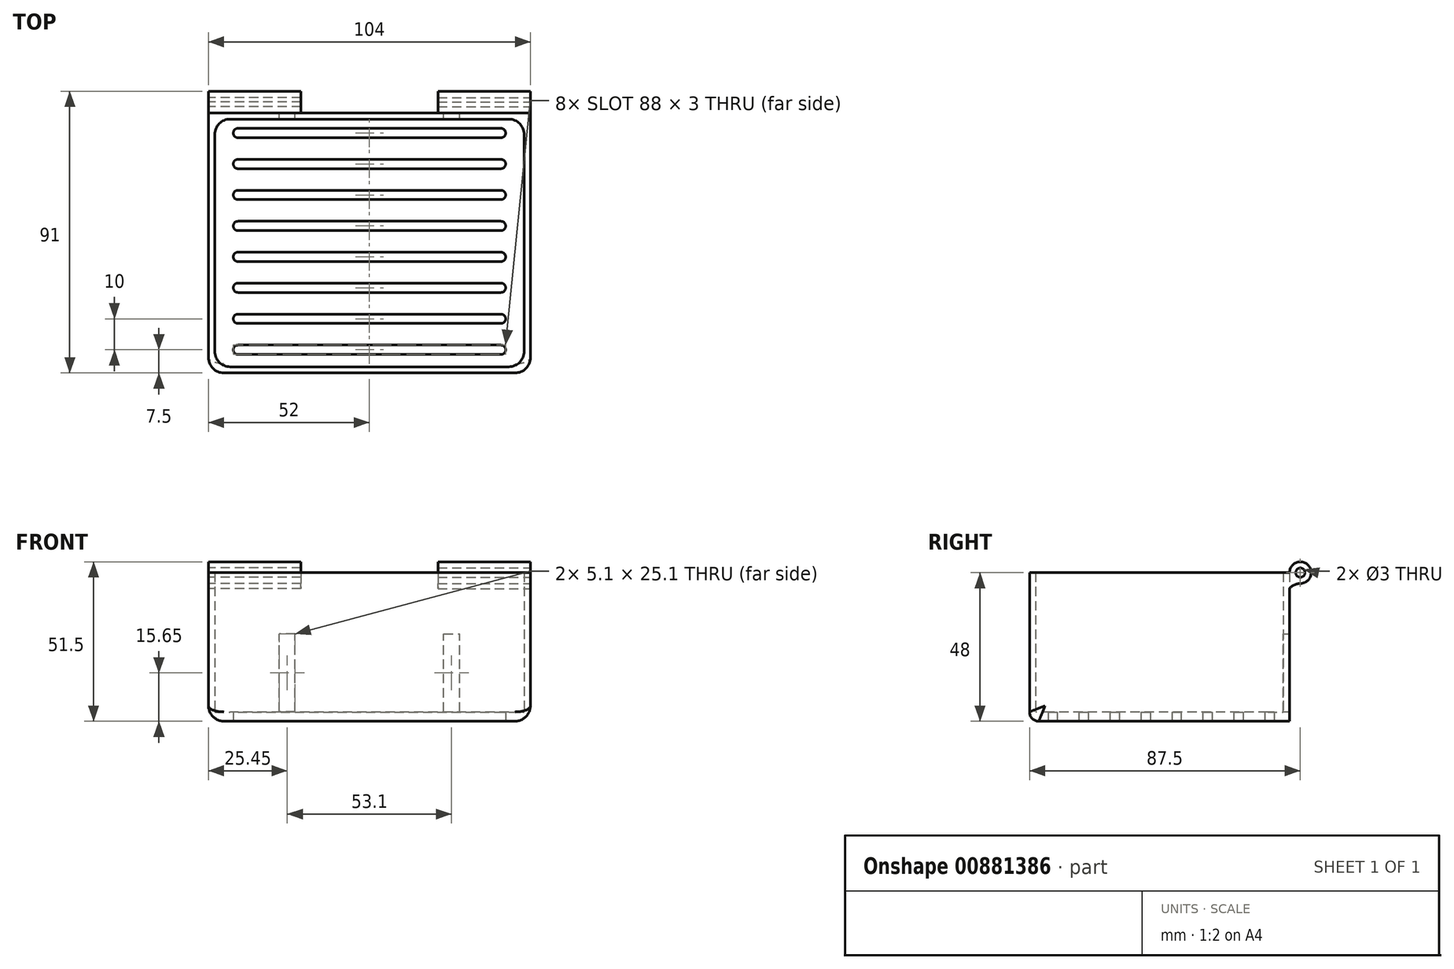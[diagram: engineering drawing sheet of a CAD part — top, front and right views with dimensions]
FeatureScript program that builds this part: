
annotation { "Feature Type Name" : "Feature", "Feature Type Description" : "" }
export const myFeature = defineFeature(function(context is Context, id is Id, definition is map)
    precondition{}
    {
        {
            var Q0;
            Q0=qCreatedBy(makeId("Top.planeOp"),FACE);
            var sketch = newSketch(context, id + "F0", { "sketchPlane" : qUnion([Q0])});
            skLineSegment(sketch, "E0.bottom", {"start": v(50, 40) * mm, "end": v(-50, 40) * mm});
            skLineSegment(sketch, "E0.top", {"start": v(50, -40) * mm, "end": v(-50, -40) * mm});
            skLineSegment(sketch, "E0.left", {"start": v(50, 40) * mm, "end": v(50, -40) * mm});
            skLineSegment(sketch, "E0.right", {"start": v(-50, 40) * mm, "end": v(-50, -40) * mm});
            skPoint(sketch, "E0.middle", {"position": v(0, 0) * mm});
            skLineSegment(sketch, "E1.bottom", {"start": v(52, 42) * mm, "end": v(-52, 42) * mm});
            skLineSegment(sketch, "E1.top", {"start": v(52, -42) * mm, "end": v(-52, -42) * mm});
            skLineSegment(sketch, "E1.left", {"start": v(52, 42) * mm, "end": v(52, -42) * mm});
            skLineSegment(sketch, "E1.right", {"start": v(-52, 42) * mm, "end": v(-52, -42) * mm});
            skLineSegment(sketch, "E2.bottom", {"start": v(-42.5, 37) * mm, "end": v(42.5, 37) * mm});
            skLineSegment(sketch, "E2.top", {"start": v(-42.5, 34) * mm, "end": v(42.5, 34) * mm});
            skPoint(sketch, "E3", {"position": v(0, 37) * mm});
            skArc(sketch, "E4", {"start": v(-42.5, 37) * mm, "mid": v(-44, 35.5) * mm, "end": v(-42.5, 34) * mm});
            skArc(sketch, "E5", {"start": v(42.5, 34) * mm, "mid": v(44, 35.5) * mm, "end": v(42.5, 37) * mm});
            skLineSegment(sketch, "E6.0.1.0", {"start": v(-42.5, 27) * mm, "end": v(42.5, 27) * mm});
            skLineSegment(sketch, "E6.0.1.1", {"start": v(-42.5, 24) * mm, "end": v(42.5, 24) * mm});
            skArc(sketch, "E6.0.1.2", {"start": v(42.5, 24) * mm, "mid": v(44, 25.5) * mm, "end": v(42.5, 27) * mm});
            skArc(sketch, "E6.0.1.3", {"start": v(-42.5, 27) * mm, "mid": v(-44, 25.5) * mm, "end": v(-42.5, 24) * mm});
            skLineSegment(sketch, "E6.0.2.0", {"start": v(-42.5, 17) * mm, "end": v(42.5, 17) * mm});
            skLineSegment(sketch, "E6.0.2.1", {"start": v(-42.5, 14) * mm, "end": v(42.5, 14) * mm});
            skArc(sketch, "E6.0.2.2", {"start": v(42.5, 14) * mm, "mid": v(44, 15.5) * mm, "end": v(42.5, 17) * mm});
            skArc(sketch, "E6.0.2.3", {"start": v(-42.5, 17) * mm, "mid": v(-44, 15.5) * mm, "end": v(-42.5, 14) * mm});
            skLineSegment(sketch, "E6.0.3.0", {"start": v(-42.5, 7) * mm, "end": v(42.5, 7) * mm});
            skLineSegment(sketch, "E6.0.3.1", {"start": v(-42.5, 4) * mm, "end": v(42.5, 4) * mm});
            skArc(sketch, "E6.0.3.2", {"start": v(42.5, 4) * mm, "mid": v(44, 5.5) * mm, "end": v(42.5, 7) * mm});
            skArc(sketch, "E6.0.3.3", {"start": v(-42.5, 7) * mm, "mid": v(-44, 5.5) * mm, "end": v(-42.5, 4) * mm});
            skLineSegment(sketch, "E6.0.4.0", {"start": v(-42.5, -3) * mm, "end": v(42.5, -3) * mm});
            skLineSegment(sketch, "E6.0.4.1", {"start": v(-42.5, -6) * mm, "end": v(42.5, -6) * mm});
            skArc(sketch, "E6.0.4.2", {"start": v(42.5, -6) * mm, "mid": v(44, -4.5) * mm, "end": v(42.5, -3) * mm});
            skArc(sketch, "E6.0.4.3", {"start": v(-42.5, -3) * mm, "mid": v(-44, -4.5) * mm, "end": v(-42.5, -6) * mm});
            skLineSegment(sketch, "E6.0.5.0", {"start": v(-42.5, -13) * mm, "end": v(42.5, -13) * mm});
            skLineSegment(sketch, "E6.0.5.1", {"start": v(-42.5, -16) * mm, "end": v(42.5, -16) * mm});
            skArc(sketch, "E6.0.5.2", {"start": v(42.5, -16) * mm, "mid": v(44, -14.5) * mm, "end": v(42.5, -13) * mm});
            skArc(sketch, "E6.0.5.3", {"start": v(-42.5, -13) * mm, "mid": v(-44, -14.5) * mm, "end": v(-42.5, -16) * mm});
            skLineSegment(sketch, "E6.0.6.0", {"start": v(-42.5, -23) * mm, "end": v(42.5, -23) * mm});
            skLineSegment(sketch, "E6.0.6.1", {"start": v(-42.5, -26) * mm, "end": v(42.5, -26) * mm});
            skArc(sketch, "E6.0.6.2", {"start": v(42.5, -26) * mm, "mid": v(44, -24.5) * mm, "end": v(42.5, -23) * mm});
            skArc(sketch, "E6.0.6.3", {"start": v(-42.5, -23) * mm, "mid": v(-44, -24.5) * mm, "end": v(-42.5, -26) * mm});
            skLineSegment(sketch, "E6.0.7.0", {"start": v(-42.5, -33) * mm, "end": v(42.5, -33) * mm});
            skLineSegment(sketch, "E6.0.7.1", {"start": v(-42.5, -36) * mm, "end": v(42.5, -36) * mm});
            skArc(sketch, "E6.0.7.2", {"start": v(42.5, -36) * mm, "mid": v(44, -34.5) * mm, "end": v(42.5, -33) * mm});
            skArc(sketch, "E6.0.7.3", {"start": v(-42.5, -33) * mm, "mid": v(-44, -34.5) * mm, "end": v(-42.5, -36) * mm});
            skLineSegment(sketch, "E6.direction1", {"start": v(-42.5, 37) * mm, "end": v(-42.3, 37) * mm, "construction": true});
            skLineSegment(sketch, "E6.direction2", {"start": v(-42.5, 37) * mm, "end": v(-42.5, 27) * mm, "construction": true});
            skSolve(sketch);
        }
        {
            var Q0;
            Q0=makeQuery(id+"F0.imprint","IMPRINT",FACE,{"disambiguationData":[TD([[makeQuery(id+"F0.imprint","IMPRINT",EDGE,{"derivedFrom":sQuery(id+"F0.wireOp",EDGE,"E0.bottom")}),1.0]])]});
            extrude(context, id + "F1", {"entities" : qUnion([Q0]), "depth" : 3 * mm, "offsetDistance" : 25 * mm});
        }
        {
            var Q0;
            Q0=makeQuery(id+"F0.imprint","IMPRINT",FACE,{"disambiguationData":[TD([[makeQuery(id+"F0.imprint","IMPRINT",EDGE,{"derivedFrom":sQuery(id+"F0.wireOp",EDGE,"E0.bottom")}),-1.0]])]});
            extrude(context, id + "F2", {"entities" : qUnion([Q0]), "operationType" : NewBodyOperationType.ADD, "depth" : 48 * mm, "offsetDistance" : 25 * mm});
        }
        {
            var Q0;
            Q0=makeQuery(id+"F2.opExtrude","SWEPT_FACE",FACE,{"disambiguationData":[OSD([sQuery(id+"F0.wireOp",EDGE,"E1.bottom")])]});
            var sketch = newSketch(context, id + "F3", { "sketchPlane" : qUnion([Q0])});
            skLineSegment(sketch, "E7", {"start": v(24, 48) * mm, "end": v(24, 0) * mm, "construction": true});
            skPoint(sketch, "E8", {"position": v(24, 3.1) * mm});
            skLineSegment(sketch, "E9.bottom", {"start": v(24, 3.1) * mm, "end": v(29.1, 3.1) * mm});
            skLineSegment(sketch, "E9.top", {"start": v(24, 28.2) * mm, "end": v(29.1, 28.2) * mm});
            skLineSegment(sketch, "E9.left", {"start": v(24, 3.1) * mm, "end": v(24, 28.2) * mm});
            skLineSegment(sketch, "E9.right", {"start": v(29.1, 3.1) * mm, "end": v(29.1, 28.2) * mm});
            skLineSegment(sketch, "E10.MirrorCS", {"start": v(-24, 3.1) * mm, "end": v(-24, 28.2) * mm});
            skLineSegment(sketch, "E11.MirrorCS", {"start": v(-24, 3.1) * mm, "end": v(-29.1, 3.1) * mm});
            skPoint(sketch, "E12.MirrorP", {"position": v(-24, 3.1) * mm});
            skLineSegment(sketch, "E13.MirrorCS", {"start": v(-24, 28.2) * mm, "end": v(-29.1, 28.2) * mm});
            skLineSegment(sketch, "E14.MirrorCS", {"start": v(-24, 48) * mm, "end": v(-24, 0) * mm, "construction": true});
            skLineSegment(sketch, "E15.MirrorCS", {"start": v(-29.1, 3.1) * mm, "end": v(-29.1, 28.2) * mm});
            skSolve(sketch);
        }
        {
            var Q0;
            Q0=makeQuery(id+"F3.imprint","IMPRINT",FACE,{"disambiguationData":[TD([[makeQuery(id+"F3.imprint","IMPRINT",EDGE,{"derivedFrom":sQuery(id+"F3.wireOp",EDGE,"E10.MirrorCS")}),1.0]])]});
            var Q1;
            Q1=makeQuery(id+"F3.imprint","IMPRINT",FACE,{"disambiguationData":[TD([[makeQuery(id+"F3.imprint","IMPRINT",EDGE,{"derivedFrom":sQuery(id+"F3.wireOp",EDGE,"E9.bottom")}),1.0]])]});
            var Q2;
            Q2=makeQuery(id+"F2.opExtrude","SWEPT_FACE",FACE,{"disambiguationData":[OSD([sQuery(id+"F0.wireOp",EDGE,"E0.bottom")])]});
            extrude(context, id + "F4", {"entities" : qUnion([Q0, Q1]), "operationType" : NewBodyOperationType.REMOVE, "endBound" : BoundingType.UP_TO_SURFACE, "oppositeDirection" : true, "depth" : 25 * mm, "endBoundEntityFace" : qUnion([Q2]), "offsetDistance" : 25 * mm});
        }
        {
            var Q0;
            Q0=makeQuery(id+"F2.opExtrude","SWEPT_EDGE",EDGE,{"disambiguationData":[OSD([sQuery(id+"F0.wireOp",EDGE,"E0.bottom"),sQuery(id+"F0.wireOp",EDGE,"E0.right")])]});
            var Q1;
            Q1=makeQuery(id+"F2.opExtrude","SWEPT_EDGE",EDGE,{"disambiguationData":[OSD([sQuery(id+"F0.wireOp",EDGE,"E0.bottom"),sQuery(id+"F0.wireOp",EDGE,"E0.left")])]});
            var Q2;
            Q2=makeQuery(id+"F2.opExtrude","SWEPT_EDGE",EDGE,{"disambiguationData":[OSD([sQuery(id+"F0.wireOp",EDGE,"E0.top"),sQuery(id+"F0.wireOp",EDGE,"E0.left")])]});
            var Q3;
            Q3=makeQuery(id+"F2.opExtrude","SWEPT_EDGE",EDGE,{"disambiguationData":[OSD([sQuery(id+"F0.wireOp",EDGE,"E0.top"),sQuery(id+"F0.wireOp",EDGE,"E0.right")])]});
            var Q4;
            Q4=makeQuery(id+"F2.opExtrude","SWEPT_EDGE",EDGE,{"disambiguationData":[OSD([sQuery(id+"F0.wireOp",EDGE,"E1.top"),sQuery(id+"F0.wireOp",EDGE,"E1.left")])]});
            var Q5;
            Q5=makeQuery(id+"F2.opExtrude","SWEPT_EDGE",EDGE,{"disambiguationData":[OSD([sQuery(id+"F0.wireOp",EDGE,"E1.top"),sQuery(id+"F0.wireOp",EDGE,"E1.right")])]});
            var Q6;
            Q6=makeQuery(id+"F1.opExtrude","CAP_EDGE",EDGE,{"disambiguationData":[OSD([sQuery(id+"F0.wireOp",EDGE,"E0.left")])],"isStart":false});
            var Q7;
            Q7=makeQuery(id+"F1.opExtrude","CAP_EDGE",EDGE,{"disambiguationData":[OSD([sQuery(id+"F0.wireOp",EDGE,"E0.right")])],"isStart":false});
            var Q8;
            Q8=makeQuery(id+"F2.opExtrude","CAP_EDGE",EDGE,{"disambiguationData":[OSD([sQuery(id+"F0.wireOp",EDGE,"E1.left")])],"isStart":true});
            var Q9;
            Q9=makeQuery(id+"F2.opExtrude","CAP_EDGE",EDGE,{"disambiguationData":[OSD([sQuery(id+"F0.wireOp",EDGE,"E1.right")])],"isStart":true});
            fillet(context, id + "F5", {"entities" : qUnion([Q0, Q1, Q2, Q3, Q4, Q5, Q6, Q7, Q8, Q9]), "radius" : 5 * mm, "tangentPropagation" : true, "allowEdgeOverflow" : false});
        }
        {
            var Q0;
            Q0=makeQuery(id+"F1.opExtrude","CAP_EDGE",EDGE,{"disambiguationData":[OSD([sQuery(id+"F0.wireOp",EDGE,"E0.bottom")])],"isStart":false});
            var Q1;
            Q1=makeQuery(id+"F1.opExtrude","CAP_EDGE",EDGE,{"disambiguationData":[OSD([sQuery(id+"F0.wireOp",EDGE,"E0.top")])],"isStart":false});
            var Q2;
            Q2=makeQuery(id+"F2.opExtrude","CAP_EDGE",EDGE,{"disambiguationData":[OSD([sQuery(id+"F0.wireOp",EDGE,"E1.top")])],"isStart":true});
            fillet(context, id + "F6", {"entities" : qUnion([Q0, Q1, Q2]), "radius" : 3 * mm, "tangentPropagation" : true, "allowEdgeOverflow" : false});
        }
        {
            var Q0;
            Q0=makeQuery(id+"F2.opExtrude","SWEPT_FACE",FACE,{"disambiguationData":[OSD([sQuery(id+"F0.wireOp",EDGE,"E1.right")])]});
            var sketch = newSketch(context, id + "F7", { "sketchPlane" : qUnion([Q0])});
            skCircle(sketch, "E16", {"center": v(-45.5, 48) * mm, "radius": 1.5 * mm});
            skArc(sketch, "E17", {"start": v(-42, 48) * mm, "mid": v(-47.97, 50.47) * mm, "end": v(-45.5, 44.5) * mm});
            skPoint(sketch, "E18", {"position": v(-42, 48) * mm});
            skPoint(sketch, "E19", {"position": v(-45.5, 44.5) * mm});
            skArc(sketch, "E20", {"start": v(-42, 42.88) * mm, "mid": v(-43.59, 44.04) * mm, "end": v(-45.5, 44.5) * mm});
            skLineSegment(sketch, "E21", {"start": v(-42, 42.88) * mm, "end": v(-42, 48) * mm});
            skSolve(sketch);
        }
        {
            var Q0;
            Q0=makeQuery(id+"F7.imprint","IMPRINT",FACE,{"disambiguationData":[TD([[makeQuery(id+"F7.imprint","IMPRINT",EDGE,{"derivedFrom":sQuery(id+"F7.wireOp",EDGE,"E16")}),-1.0]])]});
            extrude(context, id + "F8", {"entities" : qUnion([Q0]), "oppositeDirection" : true, "depth" : 29.9 * mm, "offsetDistance" : 25 * mm});
        }
        {
            var Q0;
            Q0=makeQuery(id+"F8.opExtrude","SWEPT_BODY",BODY,{"disambiguationData":[OSD([sQuery(id+"F7.wireOp",EDGE,"E16"),sQuery(id+"F7.wireOp",EDGE,"E17"),sQuery(id+"F7.wireOp",EDGE,"E20"),sQuery(id+"F7.wireOp",EDGE,"E21")])]});
            var Q1;
            Q1=qCreatedBy(makeId("Right.planeOp"),FACE);
            mirror(context, id + "F9", {"operationType" : NewBodyOperationType.ADD, "entities" : qUnion([Q0]), "mirrorPlane" : qUnion([Q1])});
        }
    });
